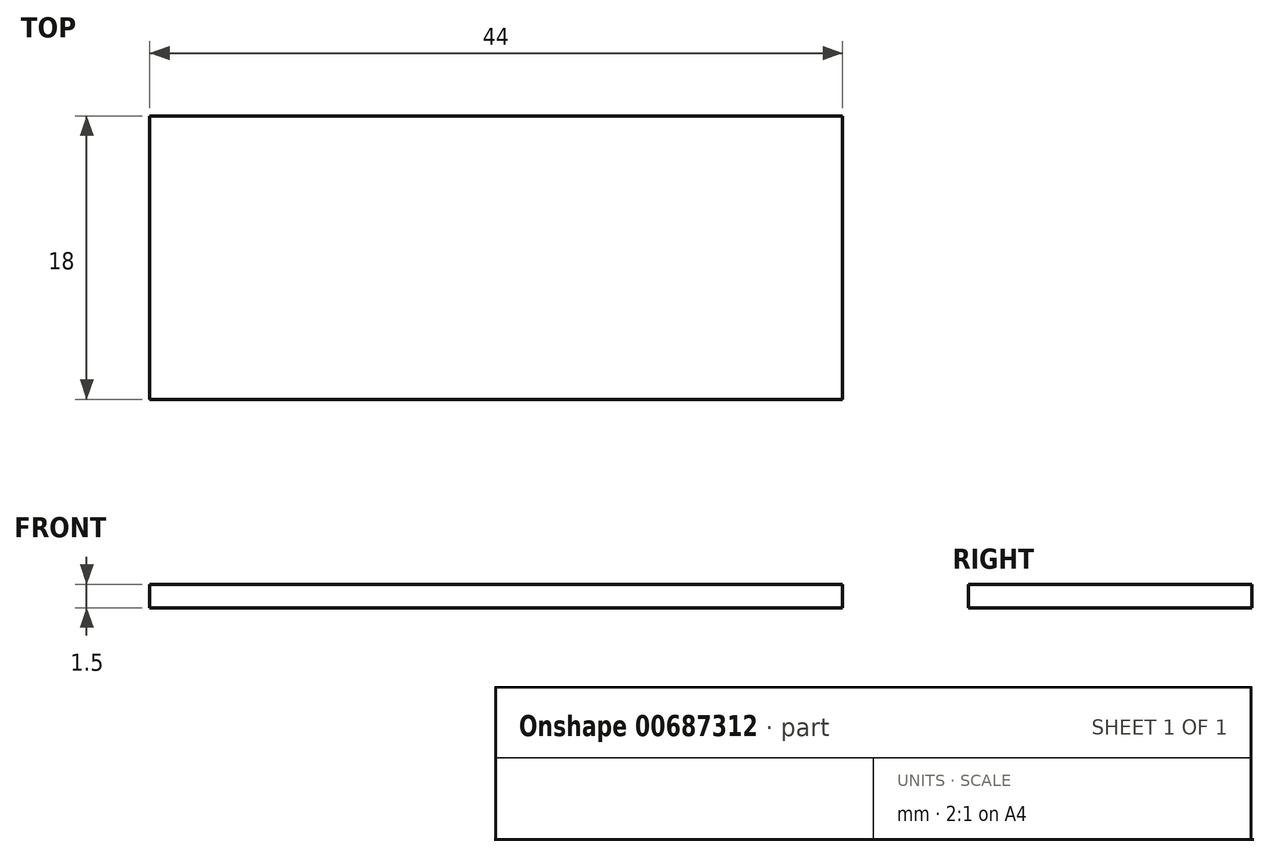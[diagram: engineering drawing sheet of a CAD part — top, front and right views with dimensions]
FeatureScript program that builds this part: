
annotation { "Feature Type Name" : "Feature", "Feature Type Description" : "" }
export const myFeature = defineFeature(function(context is Context, id is Id, definition is map)
    precondition{}
    {
        {
            var Q0;
            Q0=qCreatedBy(makeId("Top.planeOp"),FACE);
            var sketch = newSketch(context, id + "F0", { "sketchPlane" : qUnion([Q0])});
            skLineSegment(sketch, "E0.bottom", {"start": v(0, 0) * mm, "end": v(44, 0) * mm});
            skLineSegment(sketch, "E0.top", {"start": v(0, -18) * mm, "end": v(44, -18) * mm});
            skLineSegment(sketch, "E0.left", {"start": v(0, 0) * mm, "end": v(0, -18) * mm});
            skLineSegment(sketch, "E0.right", {"start": v(44, 0) * mm, "end": v(44, -18) * mm});
            skSolve(sketch);
        }
        {
            var Q0;
            Q0 = qSketchRegion(id + "F0", true);
            extrude(context, id + "F1", {"entities" : qUnion([Q0]), "depth" : 1.5 * mm, "offsetDistance" : 25 * mm});
        }
    });
